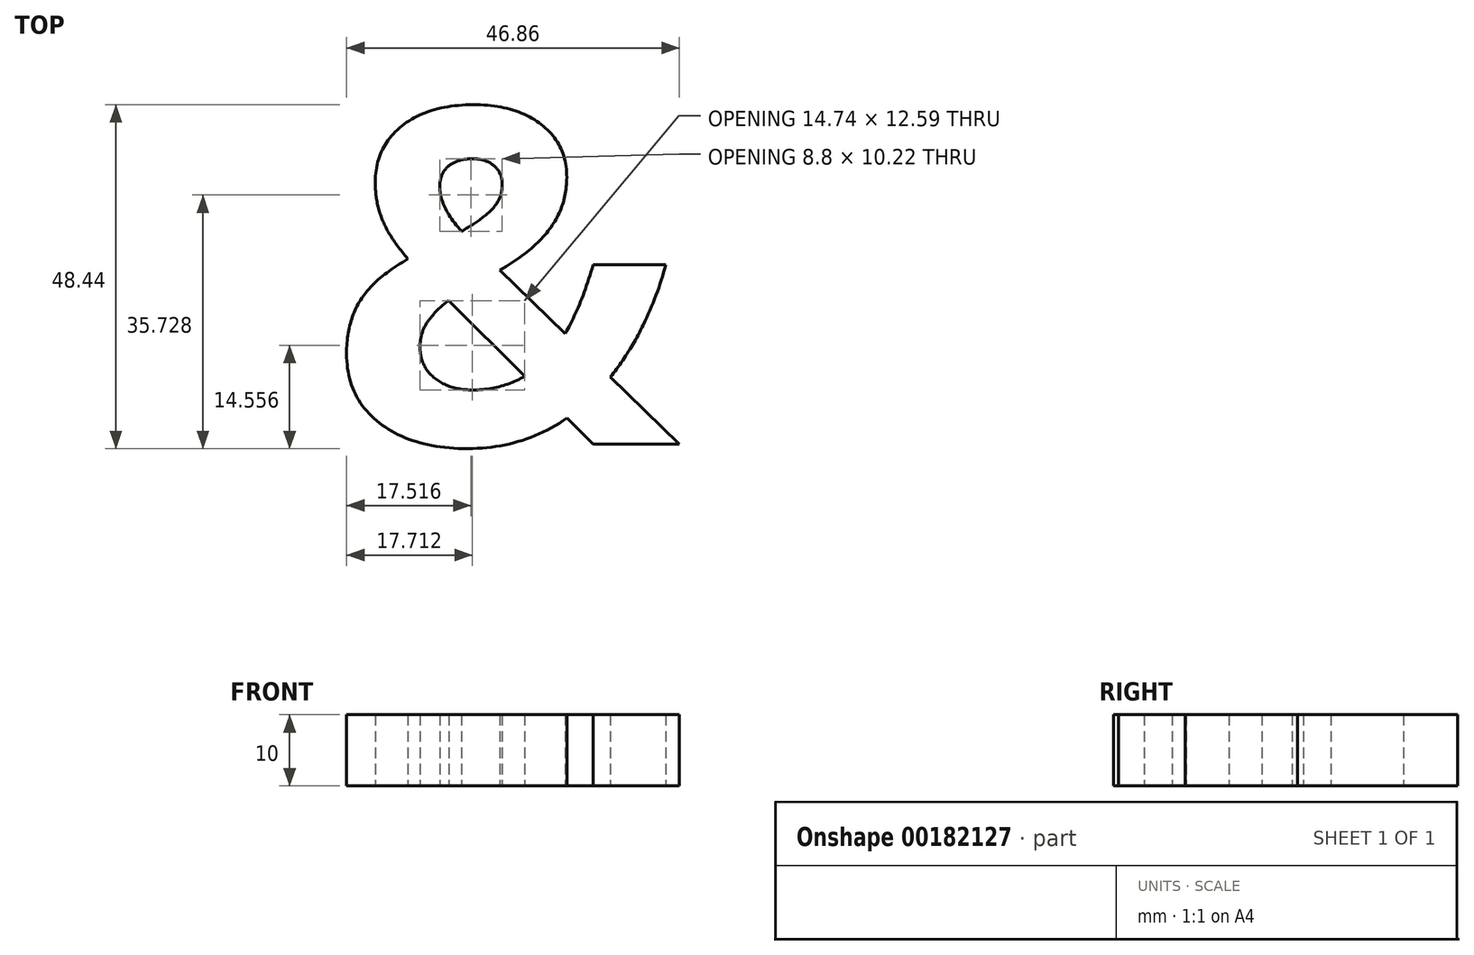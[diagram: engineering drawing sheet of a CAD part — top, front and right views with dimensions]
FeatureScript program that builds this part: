
annotation { "Feature Type Name" : "Feature", "Feature Type Description" : "" }
export const myFeature = defineFeature(function(context is Context, id is Id, definition is map)
    precondition{}
    {
        {
            var Q0;
            Q0=qCreatedBy(makeId("Top.planeOp"),FACE);
            var sketch = newSketch(context, id + "F0", { "sketchPlane" : qUnion([Q0])});
            skText(sketch, "E0", { "text": "&", "fontName": "OpenSans-Bold.ttf"});
            const initialGuessF0  = {"E0": [-0.02529, -0.02331, 1, 0, 0.04752]};
            skSetInitialGuess(sketch, initialGuessF0);
            skSolve(sketch);
        }
        {
            var Q0;
            Q0 = qSketchRegion(id + "F0", true);
            extrude(context, id + "F1", {"entities" : qUnion([Q0]), "depth" : 10 * mm});
        }
    });
